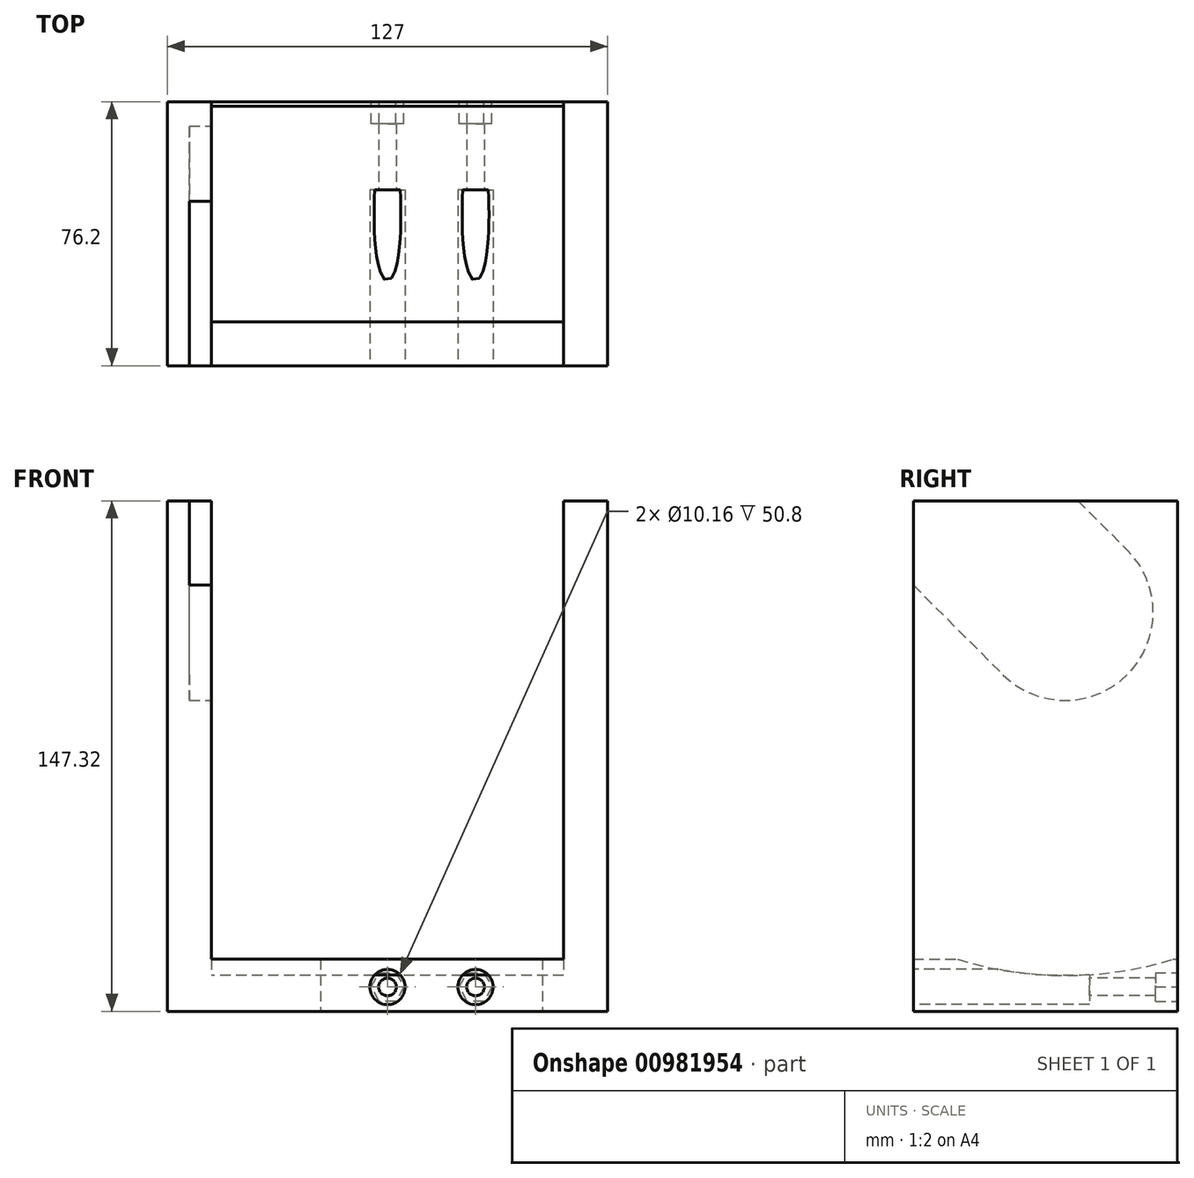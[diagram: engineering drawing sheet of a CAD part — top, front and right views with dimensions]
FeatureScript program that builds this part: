
annotation { "Feature Type Name" : "Feature", "Feature Type Description" : "" }
export const myFeature = defineFeature(function(context is Context, id is Id, definition is map)
    precondition{}
    {
        {
            var Q0;
            Q0=qCreatedBy(makeId("Top.planeOp"),FACE);
            var sketch = newSketch(context, id + "F0", { "sketchPlane" : qUnion([Q0])});
            skLineSegment(sketch, "E0.bottom", {"start": v(38.1, -38.1) * mm, "end": v(-38.1, -38.1) * mm});
            skLineSegment(sketch, "E0.top", {"start": v(38.1, 38.1) * mm, "end": v(-38.1, 38.1) * mm});
            skLineSegment(sketch, "E0.left", {"start": v(38.1, -38.1) * mm, "end": v(38.1, 38.1) * mm});
            skPoint(sketch, "E0.middle", {"position": v(0, 0) * mm});
            skLineSegment(sketch, "E1.bottom", {"start": v(-38.1, -38.1) * mm, "end": v(-63.5, -38.1) * mm});
            skLineSegment(sketch, "E1.top", {"start": v(-38.1, 38.1) * mm, "end": v(-63.5, 38.1) * mm});
            skLineSegment(sketch, "E1.right", {"start": v(-63.5, -38.1) * mm, "end": v(-63.5, 38.1) * mm});
            skSolve(sketch);
        }
        {
            var Q0;
            Q0=qSketchRegion(id+"F0",true);
            extrude(context, id + "F1", {"entities" : qUnion([Q0]), "depth" : 15 * mm, "offsetDistance" : 25.4 * mm});
        }
        {
            var Q0;
            Q0=qCreatedBy(makeId("Top.planeOp"),FACE);
            var sketch = newSketch(context, id + "F2", { "sketchPlane" : qUnion([Q0])});
            skLineSegment(sketch, "E2.bottom", {"start": v(-63.5, -38.1) * mm, "end": v(-76.2, -38.1) * mm});
            skLineSegment(sketch, "E2.top", {"start": v(-63.5, 38.1) * mm, "end": v(-76.2, 38.1) * mm});
            skLineSegment(sketch, "E2.left", {"start": v(-63.5, -38.1) * mm, "end": v(-63.5, 38.1) * mm});
            skLineSegment(sketch, "E2.right", {"start": v(-76.2, -38.1) * mm, "end": v(-76.2, 38.1) * mm});
            skLineSegment(sketch, "E3.bottom", {"start": v(38.1, -38.1) * mm, "end": v(50.8, -38.1) * mm});
            skLineSegment(sketch, "E3.top", {"start": v(38.1, 38.1) * mm, "end": v(50.8, 38.1) * mm});
            skLineSegment(sketch, "E3.left", {"start": v(38.1, -38.1) * mm, "end": v(38.1, 38.1) * mm});
            skLineSegment(sketch, "E3.right", {"start": v(50.8, -38.1) * mm, "end": v(50.8, 38.1) * mm});
            skSolve(sketch);
        }
        {
            var Q0;
            Q0=qSketchRegion(id+"F2",true);
            extrude(context, id + "F3", {"entities" : qUnion([Q0]), "operationType" : NewBodyOperationType.ADD, "depth" : 147.32 * mm, "offsetDistance" : 25.4 * mm});
        }
        {
            var Q0;
            Q0=makeQuery(id+"F3.boolean.opBoolean","MERGE",FACE,{"derivedFrom":[makeQuery(id+"F1.opExtrude","SWEPT_FACE",FACE,{"disambiguationData":[OSD([sQuery(id+"F0.wireOp",EDGE,"E0.bottom")])]}),makeQuery(id+"F3.opExtrude","SWEPT_FACE",FACE,{"disambiguationData":[OSD([sQuery(id+"F2.wireOp",EDGE,"E2.bottom")])]}),makeQuery(id+"F3.opExtrude","SWEPT_FACE",FACE,{"disambiguationData":[OSD([sQuery(id+"F2.wireOp",EDGE,"E3.bottom")])]})]});
            var sketch = newSketch(context, id + "F4", { "sketchPlane" : qUnion([Q0])});
            skCircle(sketch, "E4", {"center": v(-12.7, 7.01) * mm, "radius": 2.54 * mm});
            skCircle(sketch, "E5", {"center": v(12.7, 7.01) * mm, "radius": 2.54 * mm});
            skLineSegment(sketch, "E6", {"start": v(-12.7, 7.01) * mm, "end": v(12.7, 7.01) * mm, "construction": true});
            skLineSegment(sketch, "E7", {"start": v(0, 7.01) * mm, "end": v(0, 11.5) * mm});
            skSolve(sketch);
        }
        {
            var Q0;
            Q0=qSketchRegion(id+"F4",true);
            extrude(context, id + "F5", {"entities" : qUnion([Q0]), "operationType" : NewBodyOperationType.REMOVE, "endBound" : BoundingType.THROUGH_ALL, "oppositeDirection" : true, "depth" : 25.4 * mm, "offsetDistance" : 25.4 * mm});
        }
        {
            var Q0;
            Q0=makeQuery(id+"F3.boolean.opBoolean","MERGE",FACE,{"derivedFrom":[makeQuery(id+"F1.opExtrude","SWEPT_FACE",FACE,{"disambiguationData":[OSD([sQuery(id+"F0.wireOp",EDGE,"E0.top")])]}),makeQuery(id+"F3.opExtrude","SWEPT_FACE",FACE,{"disambiguationData":[OSD([sQuery(id+"F2.wireOp",EDGE,"E2.top")])]}),makeQuery(id+"F3.opExtrude","SWEPT_FACE",FACE,{"disambiguationData":[OSD([sQuery(id+"F2.wireOp",EDGE,"E3.top")])]})]});
            var sketch = newSketch(context, id + "F6", { "sketchPlane" : qUnion([Q0])});
            skCircle(sketch, "E8.cCircle", {"center": v(-12.7, 7.01) * mm, "radius": 4.11 * mm, "construction": true});
            skLineSegment(sketch, "E8.0", {"start": v(-10.33, 11.12) * mm, "end": v(-7.95, 7.01) * mm});
            skLineSegment(sketch, "E8.1", {"start": v(-7.95, 7.01) * mm, "end": v(-10.33, 2.9) * mm});
            skLineSegment(sketch, "E8.2", {"start": v(-10.33, 2.9) * mm, "end": v(-15.07, 2.9) * mm});
            skLineSegment(sketch, "E8.3", {"start": v(-15.07, 2.9) * mm, "end": v(-17.45, 7.01) * mm});
            skLineSegment(sketch, "E8.4", {"start": v(-17.45, 7.01) * mm, "end": v(-15.07, 11.12) * mm});
            skLineSegment(sketch, "E8.5", {"start": v(-15.07, 11.12) * mm, "end": v(-10.33, 11.12) * mm});
            skPoint(sketch, "E8.0.midPoint", {"position": v(-9.14, 9.07) * mm});
            skCircle(sketch, "E9.cCircle", {"center": v(12.7, 7.01) * mm, "radius": 4.11 * mm, "construction": true});
            skLineSegment(sketch, "E9.0", {"start": v(15.07, 11.12) * mm, "end": v(17.45, 7.01) * mm});
            skLineSegment(sketch, "E9.1", {"start": v(17.45, 7.01) * mm, "end": v(15.07, 2.9) * mm});
            skLineSegment(sketch, "E9.2", {"start": v(15.07, 2.9) * mm, "end": v(10.33, 2.9) * mm});
            skLineSegment(sketch, "E9.3", {"start": v(10.33, 2.9) * mm, "end": v(7.95, 7.01) * mm});
            skLineSegment(sketch, "E9.4", {"start": v(7.95, 7.01) * mm, "end": v(10.33, 11.12) * mm});
            skLineSegment(sketch, "E9.5", {"start": v(10.33, 11.12) * mm, "end": v(15.07, 11.12) * mm});
            skPoint(sketch, "E9.0.midPoint", {"position": v(16.26, 9.07) * mm});
            skSolve(sketch);
        }
        {
            var Q0;
            Q0=qSketchRegion(id+"F6",true);
            extrude(context, id + "F7", {"entities" : qUnion([Q0]), "operationType" : NewBodyOperationType.REMOVE, "oppositeDirection" : true, "depth" : 6.35 * mm, "offsetDistance" : 25.4 * mm});
        }
        {
            var Q0;
            Q0=makeQuery(id+"F3.boolean.opBoolean","MERGE",FACE,{"derivedFrom":[makeQuery(id+"F1.opExtrude","SWEPT_FACE",FACE,{"disambiguationData":[OSD([sQuery(id+"F0.wireOp",EDGE,"E0.bottom")])]}),makeQuery(id+"F3.opExtrude","SWEPT_FACE",FACE,{"disambiguationData":[OSD([sQuery(id+"F2.wireOp",EDGE,"E2.bottom")])]}),makeQuery(id+"F3.opExtrude","SWEPT_FACE",FACE,{"disambiguationData":[OSD([sQuery(id+"F2.wireOp",EDGE,"E3.bottom")])]})]});
            var sketch = newSketch(context, id + "F8", { "sketchPlane" : qUnion([Q0])});
            skCircle(sketch, "E10", {"center": v(-12.7, 7.01) * mm, "radius": 5.08 * mm});
            skCircle(sketch, "E11", {"center": v(12.7, 7.01) * mm, "radius": 5.08 * mm});
            skSolve(sketch);
        }
        {
            var Q0;
            Q0=qSketchRegion(id+"F8",true);
            extrude(context, id + "F9", {"entities" : qUnion([Q0]), "operationType" : NewBodyOperationType.REMOVE, "oppositeDirection" : true, "depth" : 50.8 * mm, "offsetDistance" : 25.4 * mm});
        }
        {
            var Q0;
            Q0=makeQuery(id+"F3.opExtrude","SWEPT_FACE",FACE,{"disambiguationData":[OSD([sQuery(id+"F2.wireOp",EDGE,"E2.left")])]});
            var sketch = newSketch(context, id + "F10", { "sketchPlane" : qUnion([Q0])});
            skArc(sketch, "E12", {"start": v(-12.3, 97.16) * mm, "mid": v(23.62, 97.16) * mm, "end": v(23.62, 133.08) * mm});
            skLineSegment(sketch, "E13", {"start": v(-12.3, 97.16) * mm, "end": v(-38.1, 122.96) * mm});
            skLineSegment(sketch, "E14", {"start": v(23.62, 133.08) * mm, "end": v(9.38, 147.32) * mm});
            skLineSegment(sketch, "E15", {"start": v(9.38, 147.32) * mm, "end": v(-38.1, 147.32) * mm});
            skLineSegment(sketch, "E16", {"start": v(-38.1, 147.32) * mm, "end": v(-38.1, 122.96) * mm});
            skSolve(sketch);
        }
        {
            var Q0;
            Q0=qSketchRegion(id+"F10",true);
            extrude(context, id + "F11", {"entities" : qUnion([Q0]), "operationType" : NewBodyOperationType.REMOVE, "oppositeDirection" : true, "depth" : 6.35 * mm, "offsetDistance" : 25.4 * mm, "hasSecondDirection" : true, "secondDirectionOppositeDirection" : false, "secondDirectionDepth" : 82.55 * mm});
        }
        {
            var Q0;
            Q0=makeQuery(id+"F1.opExtrude","CAP_FACE",FACE,{"disambiguationData":[OSD([sQuery(id+"F0.wireOp",EDGE,"E0.bottom"),sQuery(id+"F0.wireOp",EDGE,"E0.top"),sQuery(id+"F0.wireOp",EDGE,"E0.left"),sQuery(id+"F0.wireOp",EDGE,"E1.bottom"),sQuery(id+"F0.wireOp",EDGE,"E1.top"),sQuery(id+"F0.wireOp",EDGE,"E1.right")])],"isStart":false});
            var sketch = newSketch(context, id + "F12", { "sketchPlane" : qUnion([Q0])});
            skLineSegment(sketch, "E17", {"start": v(-12.7, 38.1) * mm, "end": v(-12.7, -38.1) * mm});
            skSolve(sketch);
        }
        {
            var Q0;
            Q0=qCreatedBy(makeId("Right.planeOp"),FACE);
            var Q1;
            Q1=sQuery(id+"F12.wireOp",EDGE,"E17");
            cPlane(context, id + "F13", {"entities" : qUnion([Q0, Q1]), "cplaneType" : CPlaneType.LINE_ANGLE, "offset" : 25.4 * mm, "angle" : 0 * degree, "width" : 152.4 * mm, "height" : 152.4 * mm});
        }
        {
            var Q0;
            Q0=qCreatedBy(id+"F13.planeOp",FACE);
            var sketch = newSketch(context, id + "F14", { "sketchPlane" : qUnion([Q0])});
            skArc(sketch, "E18", {"start": v(-36.73, 15.01) * mm, "mid": v(-5.66, 10.3) * mm, "end": v(25.4, 15.01) * mm});
            skLineSegment(sketch, "E19", {"start": v(-36.73, 15.01) * mm, "end": v(25.4, 15.01) * mm});
            skSolve(sketch);
        }
        {
            var Q0;
            Q0=qSketchRegion(id+"F14",true);
            extrude(context, id + "F15", {"entities" : qUnion([Q0]), "operationType" : NewBodyOperationType.REMOVE, "endBound" : BoundingType.SYMMETRIC, "oppositeDirection" : true, "depth" : 101.6 * mm, "offsetDistance" : 25.4 * mm});
        }
        {
            var Q0;
            Q0=makeQuery(id+"F3.boolean.opBoolean","MERGE",FACE,{"derivedFrom":[makeQuery(id+"F1.opExtrude","SWEPT_FACE",FACE,{"disambiguationData":[OSD([sQuery(id+"F0.wireOp",EDGE,"E0.top"),sQuery(id+"F0.wireOp",EDGE,"E1.top")])]}),makeQuery(id+"F3.opExtrude","SWEPT_FACE",FACE,{"disambiguationData":[OSD([sQuery(id+"F2.wireOp",EDGE,"E2.top")])]}),makeQuery(id+"F3.opExtrude","SWEPT_FACE",FACE,{"disambiguationData":[OSD([sQuery(id+"F2.wireOp",EDGE,"E3.top")])]})]});
            var sketch = newSketch(context, id + "F16", { "sketchPlane" : qUnion([Q0])});
            skLineSegment(sketch, "E20.bottom", {"start": v(-31.95, 15.01) * mm, "end": v(31.95, 15.01) * mm});
            skLineSegment(sketch, "E20.top", {"start": v(-31.95, 0) * mm, "end": v(31.95, 0) * mm});
            skLineSegment(sketch, "E20.left", {"start": v(-31.95, 15.01) * mm, "end": v(-31.95, 0) * mm});
            skLineSegment(sketch, "E20.right", {"start": v(31.95, 15.01) * mm, "end": v(31.95, 0) * mm});
            skLineSegment(sketch, "E21", {"start": v(-31.95, 7.5) * mm, "end": v(0, 7.5) * mm, "construction": true});
            skLineSegment(sketch, "E22", {"start": v(0, 7.5) * mm, "end": v(31.95, 7.5) * mm, "construction": true});
            skSolve(sketch);
        }
        {
            var Q0;
            Q0=qSketchRegion(id+"F16",true);
            extrude(context, id + "F17", {"entities" : qUnion([Q0]), "operationType" : NewBodyOperationType.REMOVE, "oppositeDirection" : true, "depth" : 0.1 * mm, "offsetDistance" : 25.4 * mm});
        }
    });
